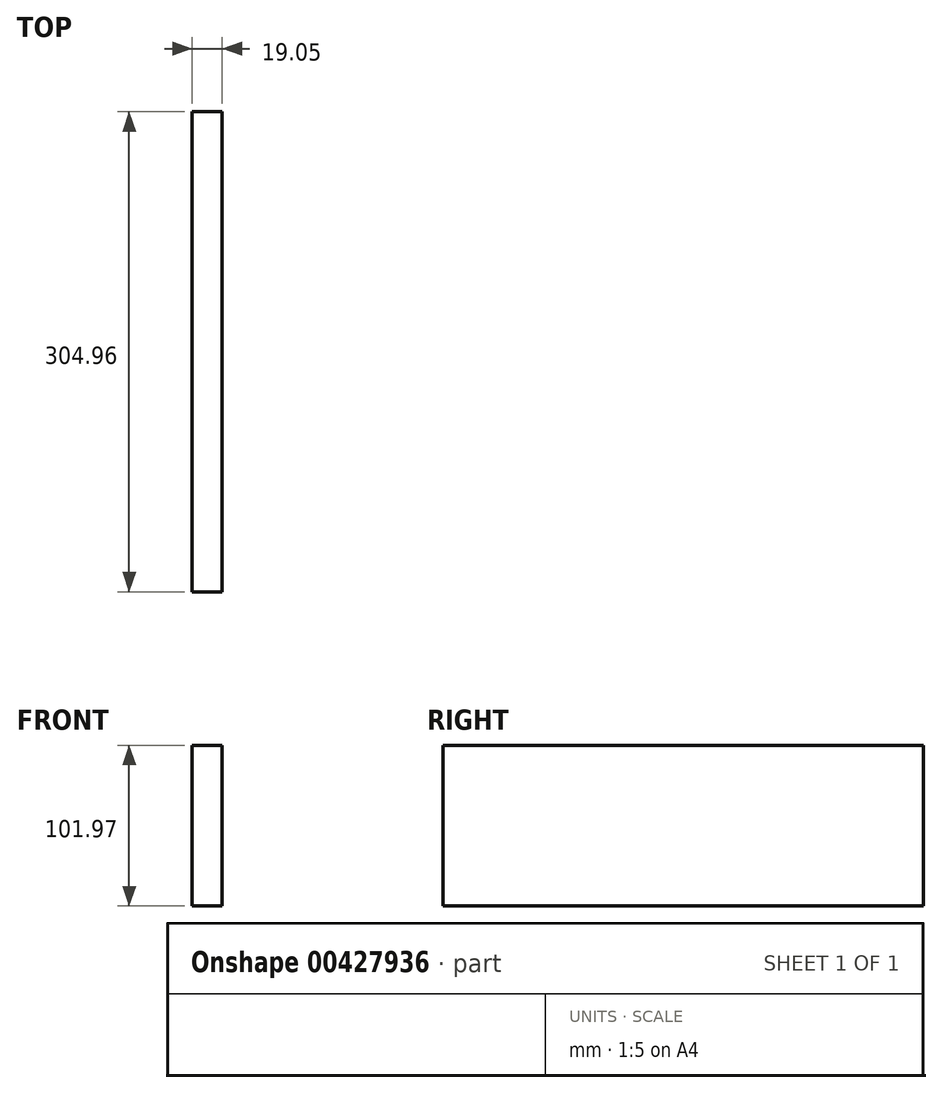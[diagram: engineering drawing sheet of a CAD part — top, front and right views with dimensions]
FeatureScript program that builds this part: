
annotation { "Feature Type Name" : "Feature", "Feature Type Description" : "" }
export const myFeature = defineFeature(function(context is Context, id is Id, definition is map)
    precondition{}
    {
        {
            var Q0;
            Q0=qCreatedBy(makeId("Right.planeOp"),FACE);
            var sketch = newSketch(context, id + "F0", { "sketchPlane" : qUnion([Q0])});
            skLineSegment(sketch, "E0.bottom", {"start": v(76.53, 74.41) * mm, "end": v(-228.43, 74.41) * mm});
            skLineSegment(sketch, "E0.top", {"start": v(76.53, -27.56) * mm, "end": v(-228.43, -27.56) * mm});
            skLineSegment(sketch, "E0.left", {"start": v(76.53, 74.41) * mm, "end": v(76.53, -27.56) * mm});
            skLineSegment(sketch, "E0.right", {"start": v(-228.43, 74.41) * mm, "end": v(-228.43, -27.56) * mm});
            skSolve(sketch);
        }
        {
            var Q0;
            Q0 = qSketchRegion(id + "F0", true);
            extrude(context, id + "F1", {"entities" : qUnion([Q0]), "depth" : 19.05 * mm});
        }
    });
